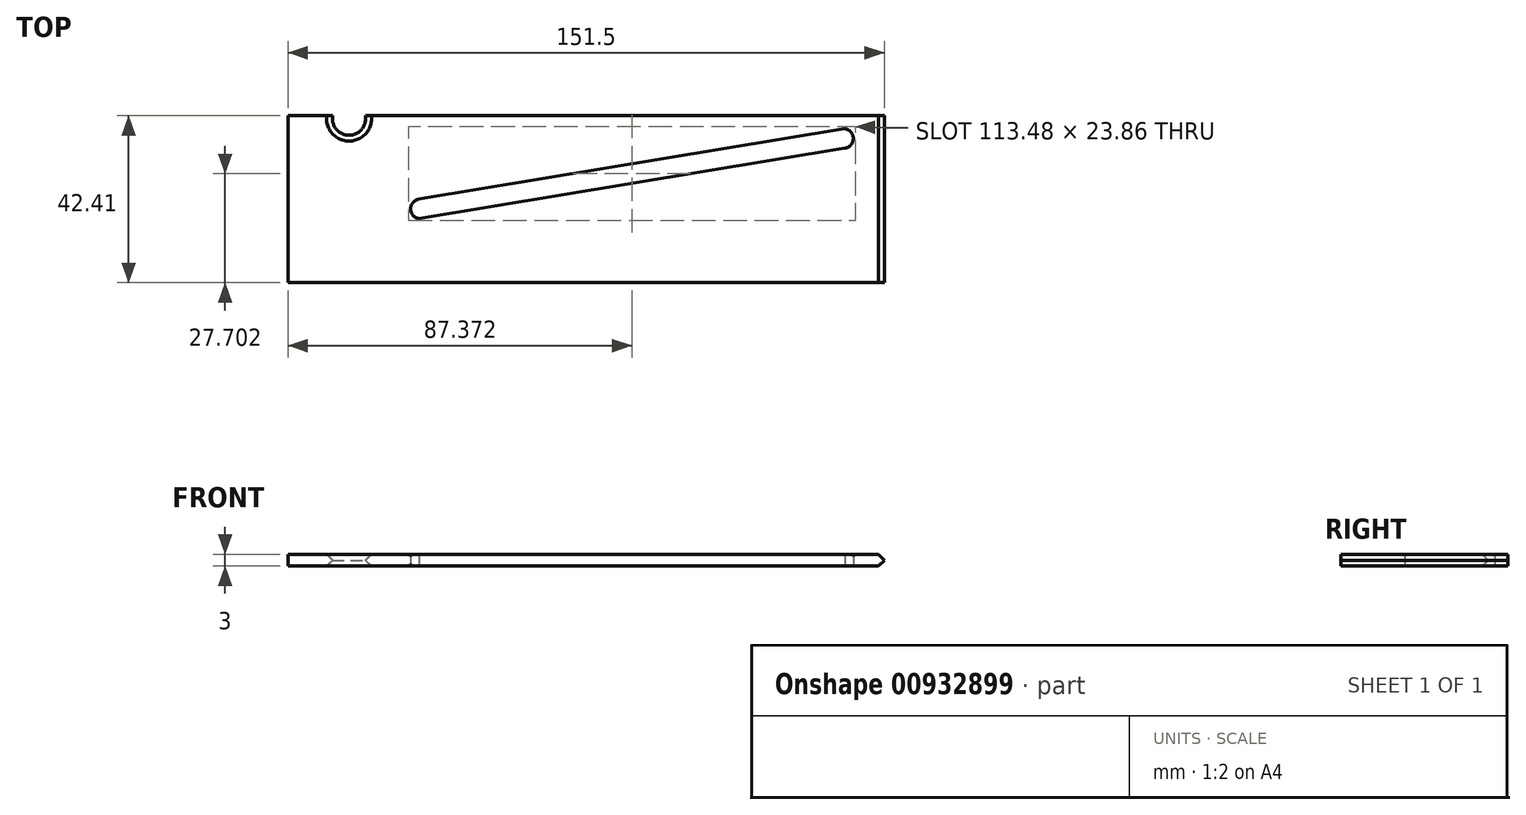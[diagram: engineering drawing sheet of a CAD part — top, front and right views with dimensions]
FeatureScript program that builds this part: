
annotation { "Feature Type Name" : "Feature", "Feature Type Description" : "" }
export const myFeature = defineFeature(function(context is Context, id is Id, definition is map)
    precondition{}
    {
        {
            var Q0;
            Q0=qCreatedBy(makeId("Top.planeOp"),FACE);
            var sketch = newSketch(context, id + "F0", { "sketchPlane" : qUnion([Q0])});
            skLineSegment(sketch, "E0.bottom", {"start": v(0, 0) * mm, "end": v(-132.86, 0) * mm});
            skLineSegment(sketch, "E0.top", {"start": v(0, 51.5) * mm, "end": v(-158.18, 51.5) * mm});
            skLineSegment(sketch, "E0.left", {"start": v(0, 0) * mm, "end": v(0, 51.5) * mm});
            skPoint(sketch, "E1.start.orphan", {"position": v(-52.76, 40.25) * mm});
            skPoint(sketch, "E2.startSnap0", {"position": v(-83.36, 40.25) * mm});
            skLineSegment(sketch, "E3.top", {"start": v(0, -42.4) * mm, "end": v(-152, -42.4) * mm});
            skLineSegment(sketch, "E3.left", {"start": v(0, 0) * mm, "end": v(0, -42.4) * mm});
            skLineSegment(sketch, "E3.right", {"start": v(-152, 0) * mm, "end": v(-152, -42.4) * mm});
            skPoint(sketch, "E4.start.orphan", {"position": v(-152, -21.2) * mm});
            skPoint(sketch, "E5.end.orphan", {"position": v(0, -21.2) * mm});
            skPoint(sketch, "E6", {"position": v(-76, -21.2) * mm});
            skPoint(sketch, "E7", {"position": v(-102.48, -26.5) * mm});
            skPoint(sketch, "E8.end.orphan", {"position": v(-106.33, 40.25) * mm});
            skPoint(sketch, "E9.end.orphan", {"position": v(-60.38, 40.25) * mm});
            skPoint(sketch, "E9.start.orphan", {"position": v(-60.38, 20.14) * mm});
            skPoint(sketch, "E10.center.orphan", {"position": v(-62.71, 20.14) * mm});
            skPoint(sketch, "E2.start.orphan", {"position": v(0, 40.25) * mm});
            skLineSegment(sketch, "E11", {"start": v(-118.78, -21.2) * mm, "end": v(-10.52, -3.28) * mm});
            skLineSegment(sketch, "E12", {"start": v(-118.74, -26.13) * mm, "end": v(-10.48, -8.21) * mm});
            skArc(sketch, "E13", {"start": v(-118.78, -21.2) * mm, "mid": v(-120.87, -23.69) * mm, "end": v(-118.74, -26.13) * mm});
            skArc(sketch, "E14", {"start": v(-10.48, -8.21) * mm, "mid": v(-8.39, -5.73) * mm, "end": v(-10.52, -3.28) * mm});
            skLineSegment(sketch, "E15", {"start": v(0, -21.2) * mm, "end": v(-18.55, -21.2) * mm});
            skLineSegment(sketch, "E16", {"start": v(-18.55, -21.2) * mm, "end": v(-18.55, 0) * mm});
            skArc(sketch, "E17", {"start": v(-140.15, 0) * mm, "mid": v(-136.5, -4.45) * mm, "end": v(-132.86, 0) * mm});
            skLineSegment(sketch, "E18.trimOffspring", {"start": v(-140.15, 0) * mm, "end": v(-152, 0) * mm});
            skSolve(sketch);
        }
        {
            var Q0;
            Q0 = qSketchRegion(id + "F0", true);
            extrude(context, id + "F1", {"entities" : qUnion([Q0]), "depth" : 3 * mm, "offsetDistance" : 25.4 * mm});
        }
        {
            var Q0;
            Q0=makeQuery(id+"F1.opExtrude","CAP_EDGE",EDGE,{"disambiguationData":[OSD([sQuery(id+"F0.wireOp",EDGE,"E17")])],"isStart":false});
            var Q1;
            Q1=makeQuery(id+"F1.opExtrude","CAP_EDGE",EDGE,{"disambiguationData":[OSD([sQuery(id+"F0.wireOp",EDGE,"E3.left")])],"isStart":false});
            var Q2;
            Q2=makeQuery(id+"F1.opExtrude","CAP_EDGE",EDGE,{"disambiguationData":[OSD([sQuery(id+"F0.wireOp",EDGE,"E17")])],"isStart":true});
            var Q3;
            Q3=makeQuery(id+"F1.opExtrude","CAP_EDGE",EDGE,{"disambiguationData":[OSD([sQuery(id+"F0.wireOp",EDGE,"E3.left")])],"isStart":true});
            chamfer(context, id + "F2", {"entities" : qUnion([Q0, Q1, Q2, Q3]), "width" : 2 * mm, "tangentPropagation" : true});
        }
        {
            var Q0;
            Q0=makeQuery(id+"F1.opExtrude","CAP_EDGE",EDGE,{"disambiguationData":[OSD([sQuery(id+"F0.wireOp",EDGE,"E11")])],"isStart":false});
            var Q1;
            Q1=makeQuery(id+"F1.opExtrude","CAP_EDGE",EDGE,{"disambiguationData":[OSD([sQuery(id+"F0.wireOp",EDGE,"E12")])],"isStart":false});
            var Q2;
            Q2=makeQuery(id+"F1.opExtrude","CAP_EDGE",EDGE,{"disambiguationData":[OSD([sQuery(id+"F0.wireOp",EDGE,"E13")])],"isStart":false});
            var Q3;
            Q3=makeQuery(id+"F1.opExtrude","CAP_EDGE",EDGE,{"disambiguationData":[OSD([sQuery(id+"F0.wireOp",EDGE,"E14")])],"isStart":false});
            var Q4;
            Q4=makeQuery(id+"F1.opExtrude","CAP_EDGE",EDGE,{"disambiguationData":[OSD([sQuery(id+"F0.wireOp",EDGE,"E11")])],"isStart":true});
            var Q5;
            Q5=makeQuery(id+"F1.opExtrude","CAP_EDGE",EDGE,{"disambiguationData":[OSD([sQuery(id+"F0.wireOp",EDGE,"E14")])],"isStart":true});
            var Q6;
            Q6=makeQuery(id+"F1.opExtrude","CAP_EDGE",EDGE,{"disambiguationData":[OSD([sQuery(id+"F0.wireOp",EDGE,"E13")])],"isStart":true});
            fillet(context, id + "F3", {"entities" : qUnion([Q0, Q1, Q2, Q3, Q4, Q5, Q6]), "radius" : 0.5 * mm, "tangentPropagation" : true, "allowEdgeOverflow" : false});
        }
    });
